# Revit family: QF_EVEREST_EGSH4
name_source: partatom
category: Specialty Equipment
revit_build: Autodesk Revit 2015 (Build: 20160512_0715(x64)
units: mm (PartAtom-declared; Revit-internal decimal feet)

## types (2) — shared parameters
Apparent Power = 0 VA
Conn Conduit = Yes
Conn Plug = NEMA 5-15P
Cycle = 60 Hz
Depth = 803 mm  [stored 2.63451 ft]
Description = UPRIGHT REACH–IN REFRIGERATOR
Foodservice Equipment Identifier = Yes
Height = 2010 mm  [stored 6.59449 ft]
Identify Quantity as Lot = Yes
Length = 1260 mm  [stored 4.13386 ft]
Manufacturer = EVEREST
Max Overcurrent Protection = 0 A
Min Ckt Ampacity = 0 A
Model = EGSH4
Number of Poles = 1
Phase = 1
Refrigerant Volume = 0.00 kip
Volts = 115 V
zero-valued in all types: Elec Conn Connection Height, Elec Conn RI Height

## per-type parameters (varying)
| type | BTUH | FL Amps | HP | Refrigerant Type | Watts | Weight in Pounds |
| QF_EVEREST_EGSH4 | 2311.0 Btu/h | 3 A | 1/3 | R290 | 345 W | 449 |
| QF_EVEREST_EGSH2 | 2612.0 Btu/h | 11 A | 1/2 | R-134A | 1265 W | 453 |

note: [stored X ft] marks values corroborated as IEEE doubles in the binary element streams (Revit-internal decimal feet)

## geometry (parser evidence)
native form markers: Sweep x4
no freeform markers — native parametric forms only
